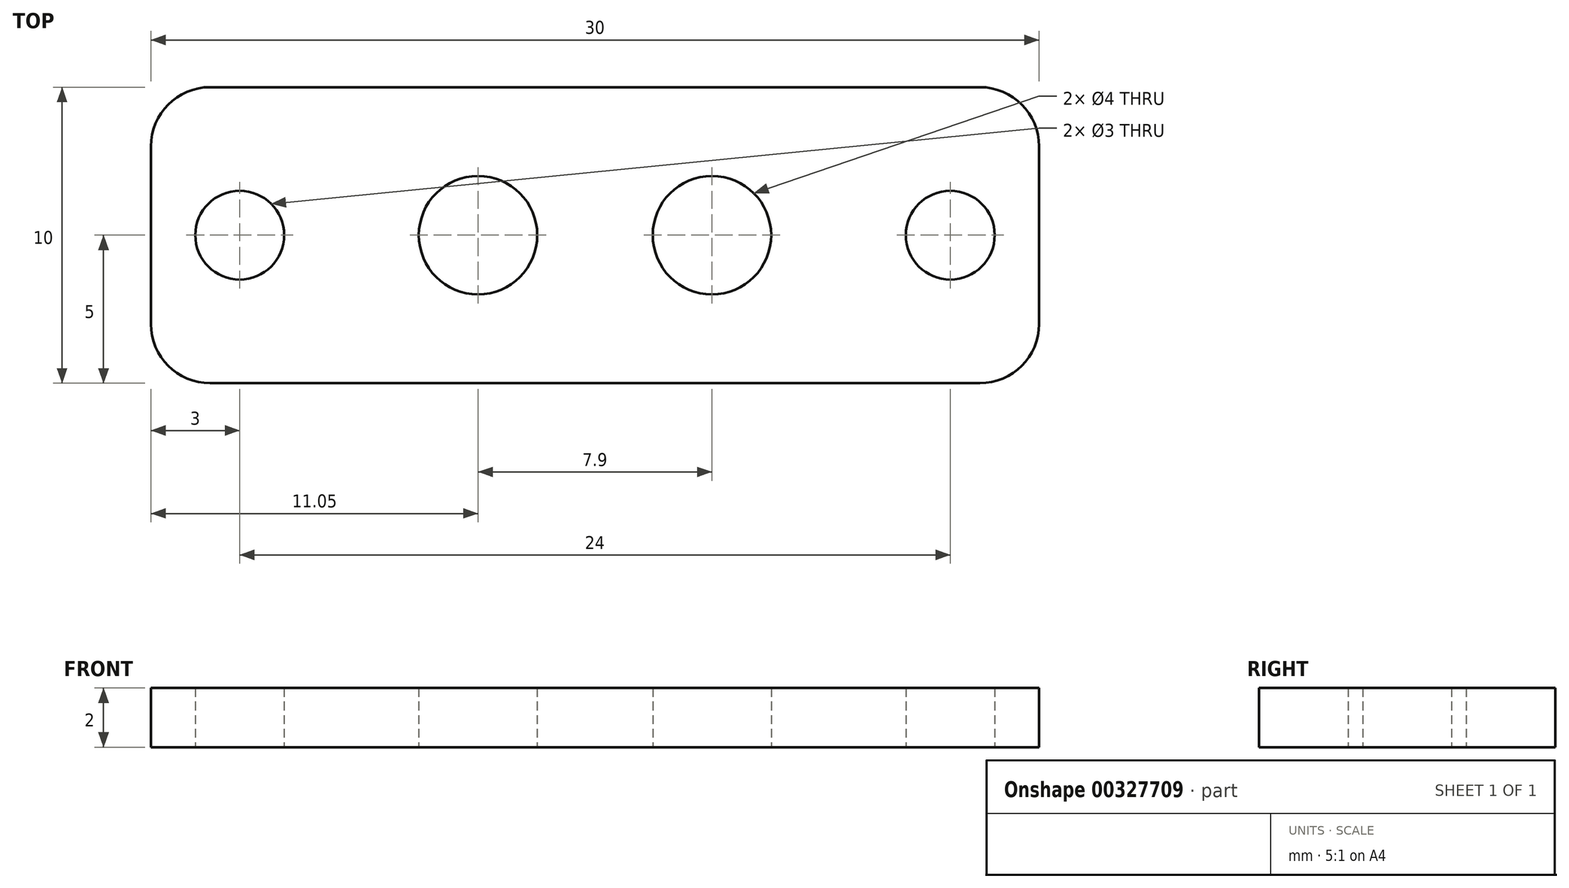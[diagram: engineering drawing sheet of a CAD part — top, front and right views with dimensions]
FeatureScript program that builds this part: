
annotation { "Feature Type Name" : "Feature", "Feature Type Description" : "" }
export const myFeature = defineFeature(function(context is Context, id is Id, definition is map)
    precondition{}
    {
        {
            var Q0;
            Q0=qCreatedBy(makeId("Top.planeOp"),FACE);
            var sketch = newSketch(context, id + "F0", { "sketchPlane" : qUnion([Q0])});
            skLineSegment(sketch, "E0.bottom", {"start": v(13, -5) * mm, "end": v(-13, -5) * mm});
            skLineSegment(sketch, "E0.top", {"start": v(13, 5) * mm, "end": v(-13, 5) * mm});
            skLineSegment(sketch, "E0.left", {"start": v(15, -3) * mm, "end": v(15, 3) * mm});
            skLineSegment(sketch, "E0.right", {"start": v(-15, -3) * mm, "end": v(-15, 3) * mm});
            skPoint(sketch, "E0.middle", {"position": v(0, 0) * mm});
            skCircle(sketch, "E1", {"center": v(-3.95, 0) * mm, "radius": 2 * mm});
            skCircle(sketch, "E2", {"center": v(-12, 0) * mm, "radius": 1.5 * mm});
            skCircle(sketch, "E3.MirrorC", {"center": v(3.95, 0) * mm, "radius": 2 * mm});
            skCircle(sketch, "E4.MirrorC", {"center": v(12, 0) * mm, "radius": 1.5 * mm});
            skPoint(sketch, "E5.visualSharp", {"position": v(-15, 5) * mm});
            skArc(sketch, "E5.filletArc", {"start": v(-13, 5) * mm, "mid": v(-14.41, 4.41) * mm, "end": v(-15, 3) * mm});
            skPoint(sketch, "E6.visualSharp", {"position": v(-15, -5) * mm});
            skArc(sketch, "E6.filletArc", {"start": v(-15, -3) * mm, "mid": v(-14.41, -4.41) * mm, "end": v(-13, -5) * mm});
            skPoint(sketch, "E7.visualSharp", {"position": v(15, -5) * mm});
            skArc(sketch, "E7.filletArc", {"start": v(13, -5) * mm, "mid": v(14.41, -4.41) * mm, "end": v(15, -3) * mm});
            skPoint(sketch, "E8.visualSharp", {"position": v(15, 5) * mm});
            skArc(sketch, "E8.filletArc", {"start": v(15, 3) * mm, "mid": v(14.41, 4.41) * mm, "end": v(13, 5) * mm});
            skLineSegment(sketch, "E9.bottom", {"start": v(5, -4) * mm, "end": v(-8, -4) * mm, "construction": true});
            skLineSegment(sketch, "E9.top", {"start": v(5, 4) * mm, "end": v(-8, 4) * mm, "construction": true});
            skLineSegment(sketch, "E9.left", {"start": v(8, -1) * mm, "end": v(8, 1) * mm, "construction": true});
            skLineSegment(sketch, "E9.right", {"start": v(-8, -4) * mm, "end": v(-8, 4) * mm, "construction": true});
            skPoint(sketch, "E10.visualSharp", {"position": v(8, -4) * mm});
            skArc(sketch, "E10.filletArc", {"start": v(5, -4) * mm, "mid": v(7.12, -3.12) * mm, "end": v(8, -1) * mm, "construction": true});
            skPoint(sketch, "E11.visualSharp", {"position": v(8, 4) * mm});
            skArc(sketch, "E11.filletArc", {"start": v(8, 1) * mm, "mid": v(7.12, 3.12) * mm, "end": v(5, 4) * mm, "construction": true});
            skSolve(sketch);
        }
        {
            var Q0;
            Q0=makeQuery(id+"F0.imprint","IMPRINT",FACE,{"disambiguationData":[TD([[makeQuery(id+"F0.imprint","IMPRINT",EDGE,{"derivedFrom":sQuery(id+"F0.wireOp",EDGE,"E0.bottom")}),-1.0]])]});
            extrude(context, id + "F1", {"entities" : qUnion([Q0]), "depth" : 2 * mm});
        }
    });
